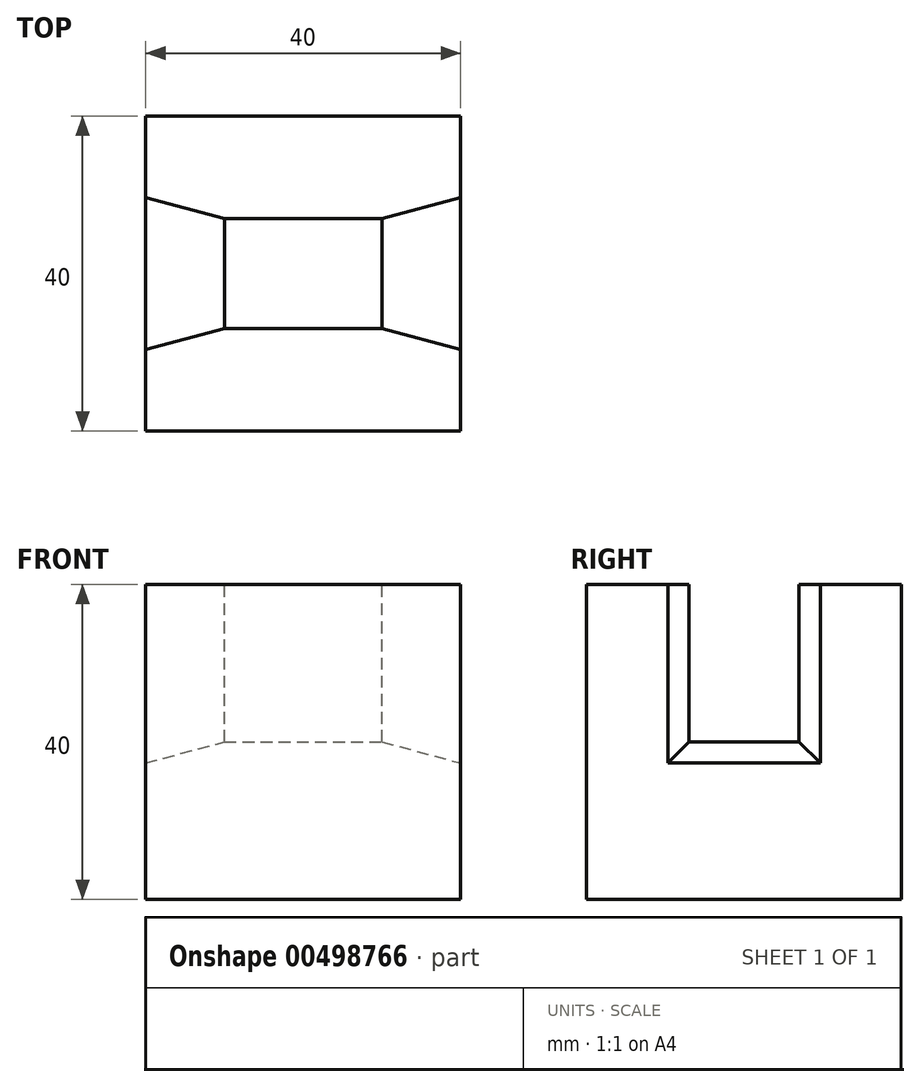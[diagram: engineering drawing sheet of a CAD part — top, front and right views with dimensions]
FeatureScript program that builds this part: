
annotation { "Feature Type Name" : "Feature", "Feature Type Description" : "" }
export const myFeature = defineFeature(function(context is Context, id is Id, definition is map)
    precondition{}
    {
        {
            var Q0;
            Q0=qCreatedBy(makeId("Front.planeOp"),FACE);
            var sketch = newSketch(context, id + "F0", { "sketchPlane" : qUnion([Q0])});
            skLineSegment(sketch, "E0.bottom", {"start": v(0, 0) * mm, "end": v(40, 0) * mm});
            skLineSegment(sketch, "E0.top", {"start": v(0, 40) * mm, "end": v(40, 40) * mm});
            skLineSegment(sketch, "E0.left", {"start": v(0, 0) * mm, "end": v(0, 40) * mm});
            skLineSegment(sketch, "E0.right", {"start": v(40, 0) * mm, "end": v(40, 40) * mm});
            skSolve(sketch);
        }
        {
            var Q0;
            Q0 = qSketchRegion(id + "F0", true);
            extrude(context, id + "F1", {"entities" : qUnion([Q0]), "depth" : 40 * mm});
        }
        {
            var Q0;
            Q0=qCreatedBy(makeId("Front.planeOp"),FACE);
            cPlane(context, id + "F2", {"entities" : qUnion([Q0]), "cplaneType" : CPlaneType.OFFSET, "offset" : 20 * mm, "width" : 150 * mm, "height" : 150 * mm});
        }
        {
            var Q0;
            Q0=qCreatedBy(id+"F2.planeOp",FACE);
            var sketch = newSketch(context, id + "F3", { "sketchPlane" : qUnion([Q0])});
            skLineSegment(sketch, "E1", {"start": v(0, 17.32) * mm, "end": v(10, 20) * mm});
            skLineSegment(sketch, "E2", {"start": v(10, 20) * mm, "end": v(30, 20) * mm});
            skLineSegment(sketch, "E3", {"start": v(30, 20) * mm, "end": v(40, 17.32) * mm});
            skLineSegment(sketch, "E4", {"start": v(20, 20) * mm, "end": v(20, 40) * mm, "construction": true});
            skLineSegment(sketch, "E5.0.0", {"start": v(40, 40) * mm, "end": v(0, 40) * mm});
            skLineSegment(sketch, "E5.0.2", {"start": v(0, 0) * mm, "end": v(40, 0) * mm});
            skLineSegment(sketch, "E6", {"start": v(0, 40) * mm, "end": v(0, 17.32) * mm});
            skLineSegment(sketch, "E7", {"start": v(40, 40) * mm, "end": v(40, 17.32) * mm});
            skSolve(sketch);
        }
        {
            var Q0;
            Q0 = qSketchRegion(id + "F3", true);
            extrude(context, id + "F4", {"entities" : qUnion([Q0]), "operationType" : NewBodyOperationType.REMOVE, "endBound" : BoundingType.SYMMETRIC, "oppositeDirection" : true, "depth" : 14 * mm});
        }
        {
            var Q0;
            {var subQ0=sQuery(id+"F0.wireOp",EDGE,"E0.right");var subQ1=sQuery(id+"F0.wireOp",EDGE,"E0.left");var subQ2=sQuery(id+"F0.wireOp",EDGE,"E0.top");Q0=makeQuery(id+"F4.boolean.opBoolean","SPLIT",FACE,{"disambiguationData":[TD([makeQuery(id+"F1.opExtrude","CAP_FACE",FACE,{"disambiguationData":[OSD([sQuery(id+"F0.wireOp",EDGE,"E0.bottom"),subQ2,subQ1,subQ0])],"isStart":false})])],"derivedFrom":makeQuery(id+"F1.opExtrude","SWEPT_FACE",FACE,{"disambiguationData":[OSD([subQ2])]})});}
            var sketch = newSketch(context, id + "F5", { "sketchPlane" : qUnion([Q0])});
            skLineSegment(sketch, "E8", {"start": v(0, -10.32) * mm, "end": v(10, -13) * mm});
            skLineSegment(sketch, "E9", {"start": v(40, -10.32) * mm, "end": v(30, -13) * mm, "construction": true});
            skLineSegment(sketch, "E10", {"start": v(0, -29.68) * mm, "end": v(10, -27) * mm});
            skLineSegment(sketch, "E11", {"start": v(40, -29.68) * mm, "end": v(30, -27) * mm, "construction": true});
            skLineSegment(sketch, "E12", {"start": v(10, -13) * mm, "end": v(0, -13) * mm});
            skLineSegment(sketch, "E13", {"start": v(0, -13) * mm, "end": v(0, -10.32) * mm});
            skLineSegment(sketch, "E14", {"start": v(10, -27) * mm, "end": v(40, -27) * mm});
            skLineSegment(sketch, "E15", {"start": v(10, -27) * mm, "end": v(0, -27) * mm});
            skLineSegment(sketch, "E16", {"start": v(0, -27) * mm, "end": v(0, -29.68) * mm});
            skSolve(sketch);
        }
        {
            var Q0;
            Q0 = qSketchRegion(id + "F5", true);
            var Q1;
            Q1=makeQuery(id+"F4.boolean.opBoolean","COPY",FACE,{"derivedFrom":makeQuery(id+"F4.opExtrude","SWEPT_FACE",FACE,{"disambiguationData":[OSD([sQuery(id+"F3.wireOp",EDGE,"E1")])]})});
            extrude(context, id + "F6", {"entities" : qUnion([Q0]), "operationType" : NewBodyOperationType.REMOVE, "endBound" : BoundingType.UP_TO_SURFACE, "oppositeDirection" : true, "endBoundEntityFace" : qUnion([Q1]), "depth" : 25 * mm});
        }
        {
            var Q0;
            {var subQ0=sQuery(id+"F0.wireOp",EDGE,"E0.right");var subQ1=sQuery(id+"F0.wireOp",EDGE,"E0.left");var subQ2=sQuery(id+"F0.wireOp",EDGE,"E0.top");Q0=makeQuery(id+"F4.boolean.opBoolean","SPLIT",FACE,{"disambiguationData":[TD([makeQuery(id+"F1.opExtrude","CAP_FACE",FACE,{"disambiguationData":[OSD([sQuery(id+"F0.wireOp",EDGE,"E0.bottom"),subQ2,subQ1,subQ0])],"isStart":true})])],"derivedFrom":makeQuery(id+"F1.opExtrude","SWEPT_FACE",FACE,{"disambiguationData":[OSD([subQ2])]})});}
            var sketch = newSketch(context, id + "F7", { "sketchPlane" : qUnion([Q0])});
            skLineSegment(sketch, "E17", {"start": v(30, -13) * mm, "end": v(40, -10.32) * mm});
            skLineSegment(sketch, "E18", {"start": v(30, -27) * mm, "end": v(40, -29.68) * mm});
            skLineSegment(sketch, "E19", {"start": v(40, -10.32) * mm, "end": v(40, -13) * mm});
            skLineSegment(sketch, "E20", {"start": v(40, -13) * mm, "end": v(30, -13) * mm});
            skLineSegment(sketch, "E21", {"start": v(30, -27) * mm, "end": v(40, -27) * mm});
            skLineSegment(sketch, "E22", {"start": v(40, -27) * mm, "end": v(40, -29.68) * mm});
            skSolve(sketch);
        }
        {
            var Q0;
            Q0 = qSketchRegion(id + "F7", true);
            var Q1;
            Q1=makeQuery(id+"F4.boolean.opBoolean","COPY",FACE,{"derivedFrom":makeQuery(id+"F4.opExtrude","SWEPT_FACE",FACE,{"disambiguationData":[OSD([sQuery(id+"F3.wireOp",EDGE,"E3")])]})});
            extrude(context, id + "F8", {"entities" : qUnion([Q0]), "operationType" : NewBodyOperationType.REMOVE, "endBound" : BoundingType.UP_TO_SURFACE, "oppositeDirection" : true, "endBoundEntityFace" : qUnion([Q1]), "depth" : 25 * mm});
        }
    });
